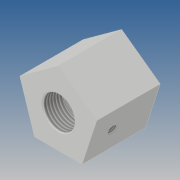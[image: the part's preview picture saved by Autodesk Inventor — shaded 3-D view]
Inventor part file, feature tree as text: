
AUTODESK INVENTOR PART (.ipt)
format: ipt  version: 2019 (Build 230136000, 136)  size: 148,480 bytes
history: native  units: mm
features: sketch x3, other x2, chamfer x2, projected_geometry x2, extrude x1, hole x1, mirror x1
ambient origin geometry x8: Origin, YZ Plane, XZ Plane, XY Plane, X Axis, Y Axis, Z Axis, Center Point
bodies: Solide1 (feature_tree)
feature tree (12):
  other  "Révolution1"
  other  "Filetage3"
  chamfer  "Chanfrein1"  Distance=10.0mm
  extrude  "Extrusion5"  Depth=12.5mm
  hole  "Perçage2"  [1 undecoded]
  mirror  "Symétrie1"
  chamfer  "Chanfrein2"  Distance=1.5mm
  sketch  "Esquisse2"
  sketch  "Esquisse7"
  projected_geometry  "Boucle projetée3"
  sketch  "Esquisse8"
  projected_geometry  "Boucle projetée4"
note: 1 required parameter value undecoded (feature->parameter linkage not recoverable at this tier; creation-order binding heuristic only, values carry confidence <= 0.55)
